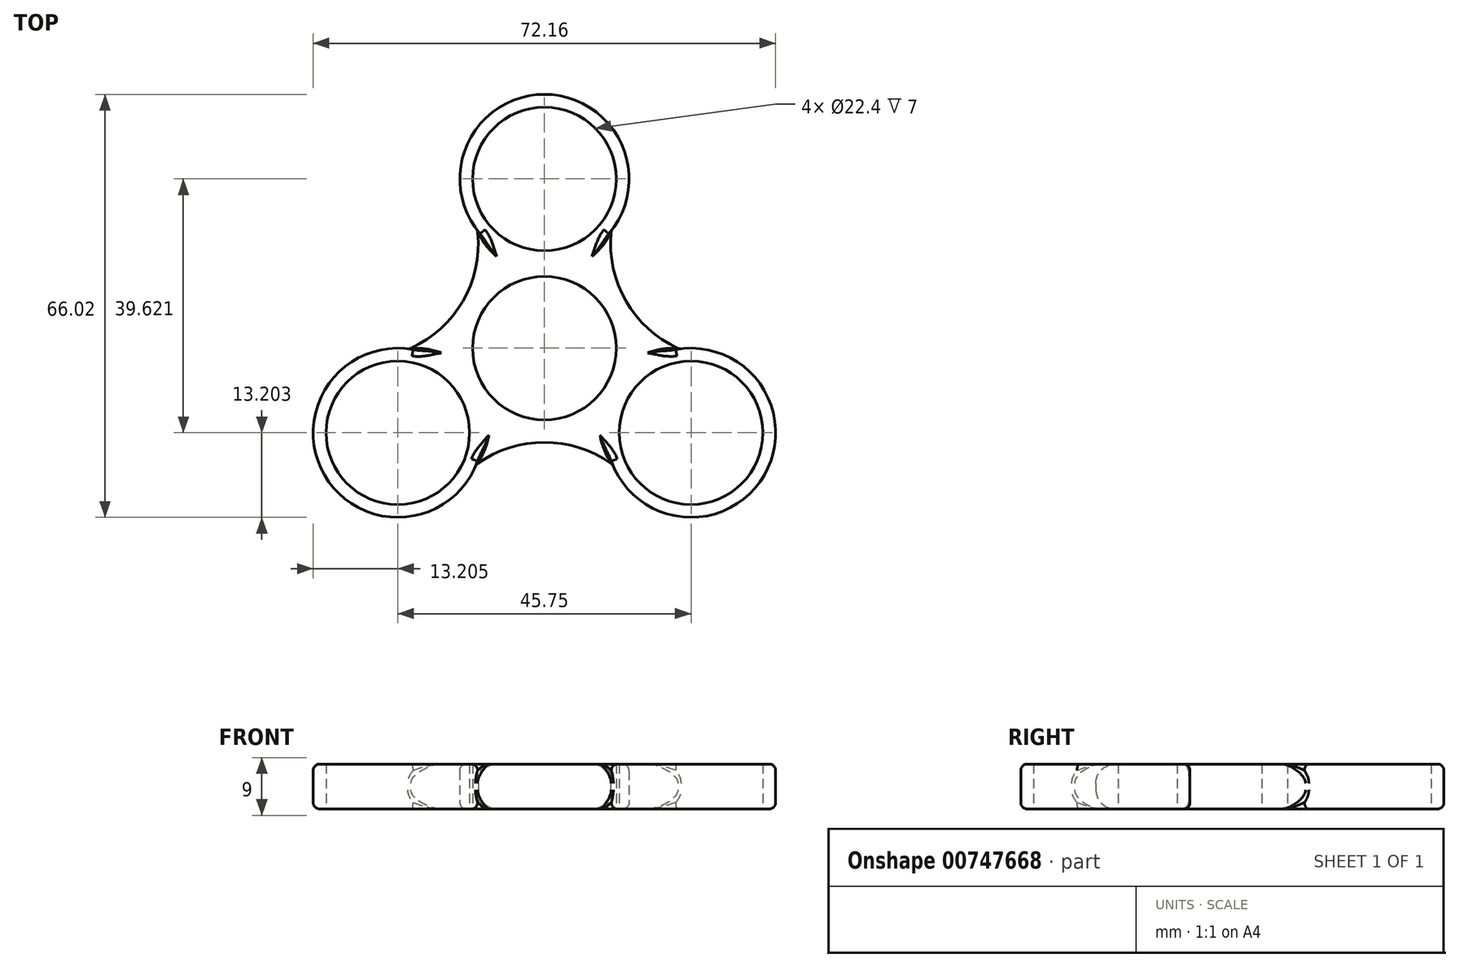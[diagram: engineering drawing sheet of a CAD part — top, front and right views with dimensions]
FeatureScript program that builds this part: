
annotation { "Feature Type Name" : "Feature", "Feature Type Description" : "" }
export const myFeature = defineFeature(function(context is Context, id is Id, definition is map)
    precondition{}
    {
        {
            var Q0;
            Q0=qCreatedBy(makeId("Top.planeOp"),FACE);
            var sketch = newSketch(context, id + "F0", { "sketchPlane" : qUnion([Q0])});
            skCircle(sketch, "E0", {"center": v(0, 0) * mm, "radius": 11.2 * mm});
            skCircle(sketch, "E1", {"center": v(0, 26.41) * mm, "radius": 11.2 * mm});
            skArc(sketch, "E2", {"start": v(10.43, 18.33) * mm, "mid": v(0, 39.61) * mm, "end": v(-10.43, 18.33) * mm});
            skCircle(sketch, "E3.1.0", {"center": v(-22.88, -13.2) * mm, "radius": 11.2 * mm});
            skArc(sketch, "E3.1.1", {"start": v(-21.09, -0.13) * mm, "mid": v(-34.3, -19.8) * mm, "end": v(-10.66, -18.2) * mm});
            skCircle(sketch, "E3.2.0", {"center": v(22.88, -13.2) * mm, "radius": 11.2 * mm});
            skArc(sketch, "E3.2.1", {"start": v(10.66, -18.2) * mm, "mid": v(34.3, -19.8) * mm, "end": v(21.09, -0.13) * mm});
            skLineSegment(sketch, "E4", {"start": v(-11.44, 6.59) * mm, "end": v(-11.44, 6.6) * mm, "construction": true});
            skPoint(sketch, "E4.startSnap0", {"position": v(-11.44, 6.6) * mm});
            skArc(sketch, "E5", {"start": v(-21.09, -0.13) * mm, "mid": v(-12.72, 7.35) * mm, "end": v(-10.43, 18.33) * mm});
            skArc(sketch, "E6.1.0", {"start": v(10.66, -18.2) * mm, "mid": v(0, -14.7) * mm, "end": v(-10.66, -18.2) * mm});
            skArc(sketch, "E6.2.0", {"start": v(10.43, 18.33) * mm, "mid": v(12.72, 7.35) * mm, "end": v(21.09, -0.13) * mm});
            skLineSegment(sketch, "E7.trimOffspring", {"start": v(-11.44, 6.6) * mm, "end": v(-11.44, 6.6) * mm, "construction": true});
            skSolve(sketch);
        }
        {
            var Q0;
            Q0=makeQuery(id+"F0.imprint","IMPRINT",FACE,{"disambiguationData":[TD([[makeQuery(id+"F0.imprint","IMPRINT",EDGE,{"derivedFrom":sQuery(id+"F0.wireOp",EDGE,"E0")}),-1.0]])]});
            extrude(context, id + "F1", {"entities" : qUnion([Q0]), "depth" : 7 * mm, "offsetDistance" : 25 * mm});
        }
        {
            var Q0;
            Q0=makeQuery(id+"F1.opExtrude","CAP_EDGE",EDGE,{"disambiguationData":[OSD([sQuery(id+"F0.wireOp",EDGE,"E5")])],"isStart":false});
            var Q1;
            Q1=makeQuery(id+"F1.opExtrude","CAP_EDGE",EDGE,{"disambiguationData":[OSD([sQuery(id+"F0.wireOp",EDGE,"E5")])],"isStart":true});
            var Q2;
            Q2=makeQuery(id+"F1.opExtrude","CAP_EDGE",EDGE,{"disambiguationData":[OSD([sQuery(id+"F0.wireOp",EDGE,"E6.2.0")])],"isStart":true});
            var Q3;
            Q3=makeQuery(id+"F1.opExtrude","CAP_EDGE",EDGE,{"disambiguationData":[OSD([sQuery(id+"F0.wireOp",EDGE,"E6.2.0")])],"isStart":false});
            var Q4;
            Q4=makeQuery(id+"F1.opExtrude","CAP_EDGE",EDGE,{"disambiguationData":[OSD([sQuery(id+"F0.wireOp",EDGE,"E6.1.0")])],"isStart":true});
            var Q5;
            Q5=makeQuery(id+"F1.opExtrude","CAP_EDGE",EDGE,{"disambiguationData":[OSD([sQuery(id+"F0.wireOp",EDGE,"E6.1.0")])],"isStart":false});
            fillet(context, id + "F2", {"entities" : qUnion([Q0, Q1, Q2, Q3, Q4, Q5]), "radius" : 3 * mm, "tangentPropagation" : true, "allowEdgeOverflow" : false});
        }
        {
            var Q0;
            Q0=makeQuery(id+"F1.opExtrude","CAP_EDGE",EDGE,{"disambiguationData":[OSD([sQuery(id+"F0.wireOp",EDGE,"E3.2.1")])],"isStart":true});
            var Q1;
            Q1=makeQuery(id+"F1.opExtrude","CAP_EDGE",EDGE,{"disambiguationData":[OSD([sQuery(id+"F0.wireOp",EDGE,"E3.2.1")])],"isStart":false});
            var Q2;
            Q2=makeQuery(id+"F2.opFillet","BLEND_EDGE",EDGE,{"blendedFrom":[makeQuery(id+"F1.opExtrude","CAP_EDGE",EDGE,{"disambiguationData":[OSD([sQuery(id+"F0.wireOp",EDGE,"E6.1.0")])],"isStart":false}),makeQuery(id+"F1.opExtrude","SWEPT_FACE",FACE,{"disambiguationData":[OSD([sQuery(id+"F0.wireOp",EDGE,"E3.2.1")])]})],"blendedInto":[makeQuery(id+"F1.opExtrude","SWEPT_FACE",FACE,{"disambiguationData":[OSD([sQuery(id+"F0.wireOp",EDGE,"E3.2.1")])]})]});
            var Q3;
            Q3=makeQuery(id+"F2.opFillet","BLEND_EDGE",EDGE,{"blendedFrom":[makeQuery(id+"F1.opExtrude","CAP_EDGE",EDGE,{"disambiguationData":[OSD([sQuery(id+"F0.wireOp",EDGE,"E6.1.0")])],"isStart":true}),makeQuery(id+"F1.opExtrude","SWEPT_FACE",FACE,{"disambiguationData":[OSD([sQuery(id+"F0.wireOp",EDGE,"E3.2.1")])]})],"blendedInto":[makeQuery(id+"F1.opExtrude","SWEPT_FACE",FACE,{"disambiguationData":[OSD([sQuery(id+"F0.wireOp",EDGE,"E3.2.1")])]})]});
            var Q4;
            Q4=makeQuery(id+"F1.opExtrude","CAP_EDGE",EDGE,{"disambiguationData":[OSD([sQuery(id+"F0.wireOp",EDGE,"E3.1.1")])],"isStart":true});
            var Q5;
            Q5=makeQuery(id+"F1.opExtrude","CAP_EDGE",EDGE,{"disambiguationData":[OSD([sQuery(id+"F0.wireOp",EDGE,"E3.1.1")])],"isStart":false});
            var Q6;
            Q6=makeQuery(id+"F2.opFillet","BLEND_EDGE",EDGE,{"blendedFrom":[makeQuery(id+"F1.opExtrude","CAP_EDGE",EDGE,{"disambiguationData":[OSD([sQuery(id+"F0.wireOp",EDGE,"E6.1.0")])],"isStart":false}),makeQuery(id+"F1.opExtrude","SWEPT_FACE",FACE,{"disambiguationData":[OSD([sQuery(id+"F0.wireOp",EDGE,"E3.1.1")])]})],"blendedInto":[makeQuery(id+"F1.opExtrude","SWEPT_FACE",FACE,{"disambiguationData":[OSD([sQuery(id+"F0.wireOp",EDGE,"E3.1.1")])]})]});
            var Q7;
            Q7=makeQuery(id+"F2.opFillet","BLEND_EDGE",EDGE,{"blendedFrom":[makeQuery(id+"F1.opExtrude","CAP_EDGE",EDGE,{"disambiguationData":[OSD([sQuery(id+"F0.wireOp",EDGE,"E6.1.0")])],"isStart":true}),makeQuery(id+"F1.opExtrude","SWEPT_FACE",FACE,{"disambiguationData":[OSD([sQuery(id+"F0.wireOp",EDGE,"E3.1.1")])]})],"blendedInto":[makeQuery(id+"F1.opExtrude","SWEPT_FACE",FACE,{"disambiguationData":[OSD([sQuery(id+"F0.wireOp",EDGE,"E3.1.1")])]})]});
            var Q8;
            Q8=makeQuery(id+"F1.opExtrude","CAP_EDGE",EDGE,{"disambiguationData":[OSD([sQuery(id+"F0.wireOp",EDGE,"E2")])],"isStart":false});
            var Q9;
            Q9=makeQuery(id+"F1.opExtrude","CAP_EDGE",EDGE,{"disambiguationData":[OSD([sQuery(id+"F0.wireOp",EDGE,"E2")])],"isStart":true});
            var Q10;
            Q10=makeQuery(id+"F2.opFillet","BLEND_EDGE",EDGE,{"blendedFrom":[makeQuery(id+"F1.opExtrude","CAP_EDGE",EDGE,{"disambiguationData":[OSD([sQuery(id+"F0.wireOp",EDGE,"E6.2.0")])],"isStart":true}),makeQuery(id+"F1.opExtrude","SWEPT_FACE",FACE,{"disambiguationData":[OSD([sQuery(id+"F0.wireOp",EDGE,"E2")])]})],"blendedInto":[makeQuery(id+"F1.opExtrude","SWEPT_FACE",FACE,{"disambiguationData":[OSD([sQuery(id+"F0.wireOp",EDGE,"E2")])]})]});
            var Q11;
            Q11=makeQuery(id+"F2.opFillet","BLEND_EDGE",EDGE,{"blendedFrom":[makeQuery(id+"F1.opExtrude","CAP_EDGE",EDGE,{"disambiguationData":[OSD([sQuery(id+"F0.wireOp",EDGE,"E6.2.0")])],"isStart":false}),makeQuery(id+"F1.opExtrude","SWEPT_FACE",FACE,{"disambiguationData":[OSD([sQuery(id+"F0.wireOp",EDGE,"E2")])]})],"blendedInto":[makeQuery(id+"F1.opExtrude","SWEPT_FACE",FACE,{"disambiguationData":[OSD([sQuery(id+"F0.wireOp",EDGE,"E2")])]})]});
            var Q12;
            Q12=makeQuery(id+"F1.opExtrude","SWEPT_EDGE",EDGE,{"disambiguationData":[OSD([sQuery(id+"F0.wireOp",EDGE,"E2"),sQuery(id+"F0.wireOp",EDGE,"E6.2.0")])]});
            var Q13;
            Q13=makeQuery(id+"F1.opExtrude","SWEPT_EDGE",EDGE,{"disambiguationData":[OSD([sQuery(id+"F0.wireOp",EDGE,"E2"),sQuery(id+"F0.wireOp",EDGE,"E5")])]});
            var Q14;
            Q14=makeQuery(id+"F2.opFillet","BLEND_EDGE",EDGE,{"blendedFrom":[makeQuery(id+"F1.opExtrude","CAP_EDGE",EDGE,{"disambiguationData":[OSD([sQuery(id+"F0.wireOp",EDGE,"E6.2.0")])],"isStart":false}),makeQuery(id+"F1.opExtrude","SWEPT_FACE",FACE,{"disambiguationData":[OSD([sQuery(id+"F0.wireOp",EDGE,"E3.2.1")])]})],"blendedInto":[makeQuery(id+"F1.opExtrude","SWEPT_FACE",FACE,{"disambiguationData":[OSD([sQuery(id+"F0.wireOp",EDGE,"E3.2.1")])]})]});
            var Q15;
            Q15=makeQuery(id+"F2.opFillet","BLEND_EDGE",EDGE,{"blendedFrom":[makeQuery(id+"F1.opExtrude","CAP_EDGE",EDGE,{"disambiguationData":[OSD([sQuery(id+"F0.wireOp",EDGE,"E6.2.0")])],"isStart":true}),makeQuery(id+"F1.opExtrude","SWEPT_FACE",FACE,{"disambiguationData":[OSD([sQuery(id+"F0.wireOp",EDGE,"E3.2.1")])]})],"blendedInto":[makeQuery(id+"F1.opExtrude","SWEPT_FACE",FACE,{"disambiguationData":[OSD([sQuery(id+"F0.wireOp",EDGE,"E3.2.1")])]})]});
            var Q16;
            Q16=makeQuery(id+"F1.opExtrude","SWEPT_EDGE",EDGE,{"disambiguationData":[OSD([sQuery(id+"F0.wireOp",EDGE,"E3.2.1"),sQuery(id+"F0.wireOp",EDGE,"E6.2.0")])]});
            var Q17;
            Q17=makeQuery(id+"F2.opFillet","BLEND_EDGE",EDGE,{"blendedFrom":[makeQuery(id+"F1.opExtrude","CAP_EDGE",EDGE,{"disambiguationData":[OSD([sQuery(id+"F0.wireOp",EDGE,"E5")])],"isStart":false}),makeQuery(id+"F1.opExtrude","SWEPT_FACE",FACE,{"disambiguationData":[OSD([sQuery(id+"F0.wireOp",EDGE,"E2")])]})],"blendedInto":[makeQuery(id+"F1.opExtrude","SWEPT_FACE",FACE,{"disambiguationData":[OSD([sQuery(id+"F0.wireOp",EDGE,"E2")])]})]});
            var Q18;
            Q18=makeQuery(id+"F2.opFillet","BLEND_EDGE",EDGE,{"blendedFrom":[makeQuery(id+"F1.opExtrude","CAP_EDGE",EDGE,{"disambiguationData":[OSD([sQuery(id+"F0.wireOp",EDGE,"E5")])],"isStart":true}),makeQuery(id+"F1.opExtrude","SWEPT_FACE",FACE,{"disambiguationData":[OSD([sQuery(id+"F0.wireOp",EDGE,"E2")])]})],"blendedInto":[makeQuery(id+"F1.opExtrude","SWEPT_FACE",FACE,{"disambiguationData":[OSD([sQuery(id+"F0.wireOp",EDGE,"E2")])]})]});
            var Q19;
            Q19=makeQuery(id+"F2.opFillet","BLEND_EDGE",EDGE,{"blendedFrom":[makeQuery(id+"F1.opExtrude","CAP_EDGE",EDGE,{"disambiguationData":[OSD([sQuery(id+"F0.wireOp",EDGE,"E5")])],"isStart":true}),makeQuery(id+"F1.opExtrude","SWEPT_FACE",FACE,{"disambiguationData":[OSD([sQuery(id+"F0.wireOp",EDGE,"E3.1.1")])]})],"blendedInto":[makeQuery(id+"F1.opExtrude","SWEPT_FACE",FACE,{"disambiguationData":[OSD([sQuery(id+"F0.wireOp",EDGE,"E3.1.1")])]})]});
            var Q20;
            Q20=makeQuery(id+"F2.opFillet","BLEND_EDGE",EDGE,{"blendedFrom":[makeQuery(id+"F1.opExtrude","CAP_EDGE",EDGE,{"disambiguationData":[OSD([sQuery(id+"F0.wireOp",EDGE,"E5")])],"isStart":false}),makeQuery(id+"F1.opExtrude","SWEPT_FACE",FACE,{"disambiguationData":[OSD([sQuery(id+"F0.wireOp",EDGE,"E3.1.1")])]})],"blendedInto":[makeQuery(id+"F1.opExtrude","SWEPT_FACE",FACE,{"disambiguationData":[OSD([sQuery(id+"F0.wireOp",EDGE,"E3.1.1")])]})]});
            var Q21;
            Q21=makeQuery(id+"F1.opExtrude","SWEPT_EDGE",EDGE,{"disambiguationData":[OSD([sQuery(id+"F0.wireOp",EDGE,"E3.1.1"),sQuery(id+"F0.wireOp",EDGE,"E5")])]});
            fillet(context, id + "F3", {"entities" : qUnion([Q0, Q1, Q2, Q3, Q4, Q5, Q6, Q7, Q8, Q9, Q10, Q11, Q12, Q13, Q14, Q15, Q16, Q17, Q18, Q19, Q20, Q21]), "radius" : 1 * mm, "tangentPropagation" : true, "allowEdgeOverflow" : false});
        }
    });
